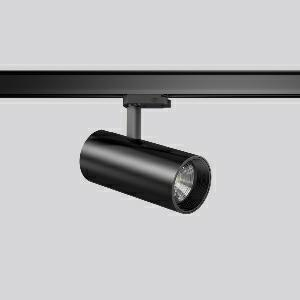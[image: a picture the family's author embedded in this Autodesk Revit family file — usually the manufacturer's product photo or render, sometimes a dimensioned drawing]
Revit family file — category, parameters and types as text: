
# Revit family: deecos_s_mini_742209_003_2_4106
name_source: partatom
category: Lighting Fixtures
units: mm (PartAtom-declared; Revit-internal decimal feet)

## family parameters
Cut with Voids When Loaded = No
Host = Face
Light Source = No
Part Type = Normal
Room Calculation Point = No
Round Connector Dimension = Use Diameter
Shared = No

## types (1)
- DEECOS S mini (1 x LED Modul 927, 3050 lm, 2700)
    Apparent Load = 29 VA
    Approval mark = CE
    CIE Flux Codes = 80 99 100 100 100
    Color Rendering = 92
    Color Temperature = 2700
    Default Elevation = 1800 mm
    Description = Series: DEECOS S mini
LED surface-mounted projector in modern design with no visible cooling ribs. Housing: die-cast aluminium, powder-coated. Rotation range: 356°. Swivel range: 90°. Black plastic ring and recessed LED to prevent glare from the side. Optical assembly with lens made of plastic (polycarbonate) for the best homogeneous light distribution - can be changed without tools. Best colour rendering index Ra>90. With multi adaptor for 3-circuit tracks 230 V. Suitable for Track on ceiling, Wall track. High quality converter without flickering and stroboscopic effect. The following accessories can be mounted without use of tools: interchangeable lenses, decorative glasses, honeycomb louvre, clear and frosted diffusers, white interchangeable plastic ring. 
Colour: deep black, matt (RAL 9005)
Diameter: 87 mm
Height: 214 mm
Lamp: LED
Socket: without socket
Colour temperature: 2700K
Colour rendering index (CRI): 92
System power: 29 W
Rated luminous flux: 3050 lm
Luminous efficiency: 105 lm/W
Control gear: Regulated power supply
Protection class: I
Type of protection: IP 20
    Height = 214 mm
    Lamp = 1 x LED Modul 927
    Lamp Light Flux = 3050 lm
    Lamp count = 1
    Length = 87 mm
    Lifetime = 50000 h
    Luminous efficacy = 105 lm/W
    Manufacturer = RZB
    ModVariant = No
    Model = 742209.003.2
    Mounting Place = Ceiling
    Mounting Type = Rail mounted
    Number of Poles = 1
    OnlyDefault = Yes
    Power Factor = 1
    Product Name = DEECOS S mini
    Product group = Track mounted projectors
    ProductGroupID = 301
    Protection Class = Protection class I
    Protection Degree = IP 20
    RLX_Detail_Level = 1
    RLX_Emergency_Light_Flux = 0 lm
    RLX_Emergency_Type = 0
    RLX_Emergency_Type_DB = No
    RlxData = <blob elided: 38877 chars, md5=96e4c034>
    Socket = socket
    Standby Power = 0 W
    System Light Flux = 3050 lm
    System Power = 29 W
    Type Comments = Product without accessories
    Type Image = 741930.003.jpg
    URL = http://relux.com
    VarID = ---
    Voltage = 230 V
    Voltage Range = 220-240 V
    Weight = 0.00 kg
    Width = 0 mm  [stored 0 ft]

note: [stored X ft] marks values corroborated as IEEE doubles in the binary element streams (Revit-internal decimal feet)

## geometry (parser evidence)
native form markers: Blend x4, Sweep x12
no freeform markers — native parametric forms only
